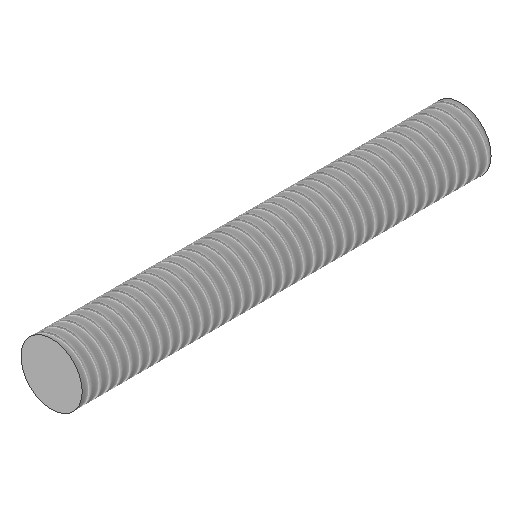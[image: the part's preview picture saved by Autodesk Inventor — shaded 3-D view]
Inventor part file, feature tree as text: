
AUTODESK INVENTOR PART (.ipt)
format: ipt  version: 2025.1 (Build 291241000, 241)  size: 137,216 bytes
history: native  units: mm
features: other x1, extrude x1, thread x1, sketch x1
ambient origin geometry x8: Origin, YZ Plane, XZ Plane, XY Plane, X Axis, Y Axis, Z Axis, Center Point
bodies: Body1 (feature_tree)
feature tree (4):
  other  "Bryła1"
  extrude  "Wyciągnięcie proste1"  Depth=3.0mm
  thread  "Gwint1"
  sketch  "Szkic1"
